# Revit family: Секция смешения - подмес сверху LITENED CV
name_source: partatom
category: Оборудование
revit_build: Autodesk Revit 2017 (Build: 20160225_1515(x64)
units: mm (PartAtom-declared; Revit-internal decimal feet)

## family parameters
Всегда вертикально = Да
На основе рабочей плоскости = Нет
Общий = Нет
При загрузке вырезать с полостями = Нет
Размер круглого соединителя = Использовать диаметр
Тип детали = Нормальный
Точка расчета площади = Нет

## types (8) — shared parameters
h = 60 мм
Единица измерения = шт.
Завод изготовитель = NED
Ключевая пометка = Вентиляция
Наименование и тех.хар-ка = Секция смешения - подмес сверху
Раздел = ОВ
высота ножек = 50 мм
zero-valued in all types: Мощность, кВт

## per-type parameters (varying)
| type | А | А1 | Б | Б1 | В1 | Г | Г1 | Д | Д1 | Масса единицы | Материал | Тип, марка, обозначение | размер В |
| CV 50-25 | 710 мм | 690 мм | 470 мм | 450 мм | 635 мм | 395 мм | 395 мм | 470 мм | 450 мм | 16 | Сталь серая | LITENED 50-25 CV | 635 мм |
| CV 50-30 | 710 мм | 690 мм | 520 мм | 500 мм | 635 мм | 445 мм | 445 мм | 520 мм | 500 мм | 18 | Сталь серая | LITENED 50-30 CV | 635 мм |
| CV 60-30 | 810 мм | 790 мм | 520 мм | 500 мм | 735 мм | 445 мм | 445 мм | 520 мм | 500 мм | 19.5 | Сталь серая | LITENED 60-30 CV | 735 мм |
| CV 60-35 | 810 мм | 790 мм | 570 мм | 550 мм | 735 мм | 495 мм | 495 мм | 570 мм | 550 мм | 21.5 | Сталь серая | LITENED 60-35 CV | 735 мм |
| CV 70-40 | 910 мм | 890 мм | 620 мм | 600 мм | 835 мм | 545 мм | 545 мм | 620 мм | 600 мм | 24.5 | Сталь серая | LITENED 70-40 CV | 835 мм |
| CV 80-50 | 1010 мм | 990 мм | 720 мм | 700 мм | 935 мм | 645 мм | 645 мм | 720 мм | 700 мм | 30 | Сталь серая | LITENED 80-50 CV | 935 мм |
| CV 90-50 | 1125 мм | 1105 мм | 740 мм | 720 мм | 1050 мм | 645 мм | 665 мм | 740 мм | 720 мм | 33.5 | Сталь серая | LITENED 90-50 CV | 1050 мм |
| CV 100-50 | 1225 мм | 1205 мм | 740 мм | 720 мм | 1150 мм | 665 мм | 665 мм | 740 мм | 720 мм | 35 | RAL 0000 Серый металл | LITENED 100-50 CV | 1150 мм |
